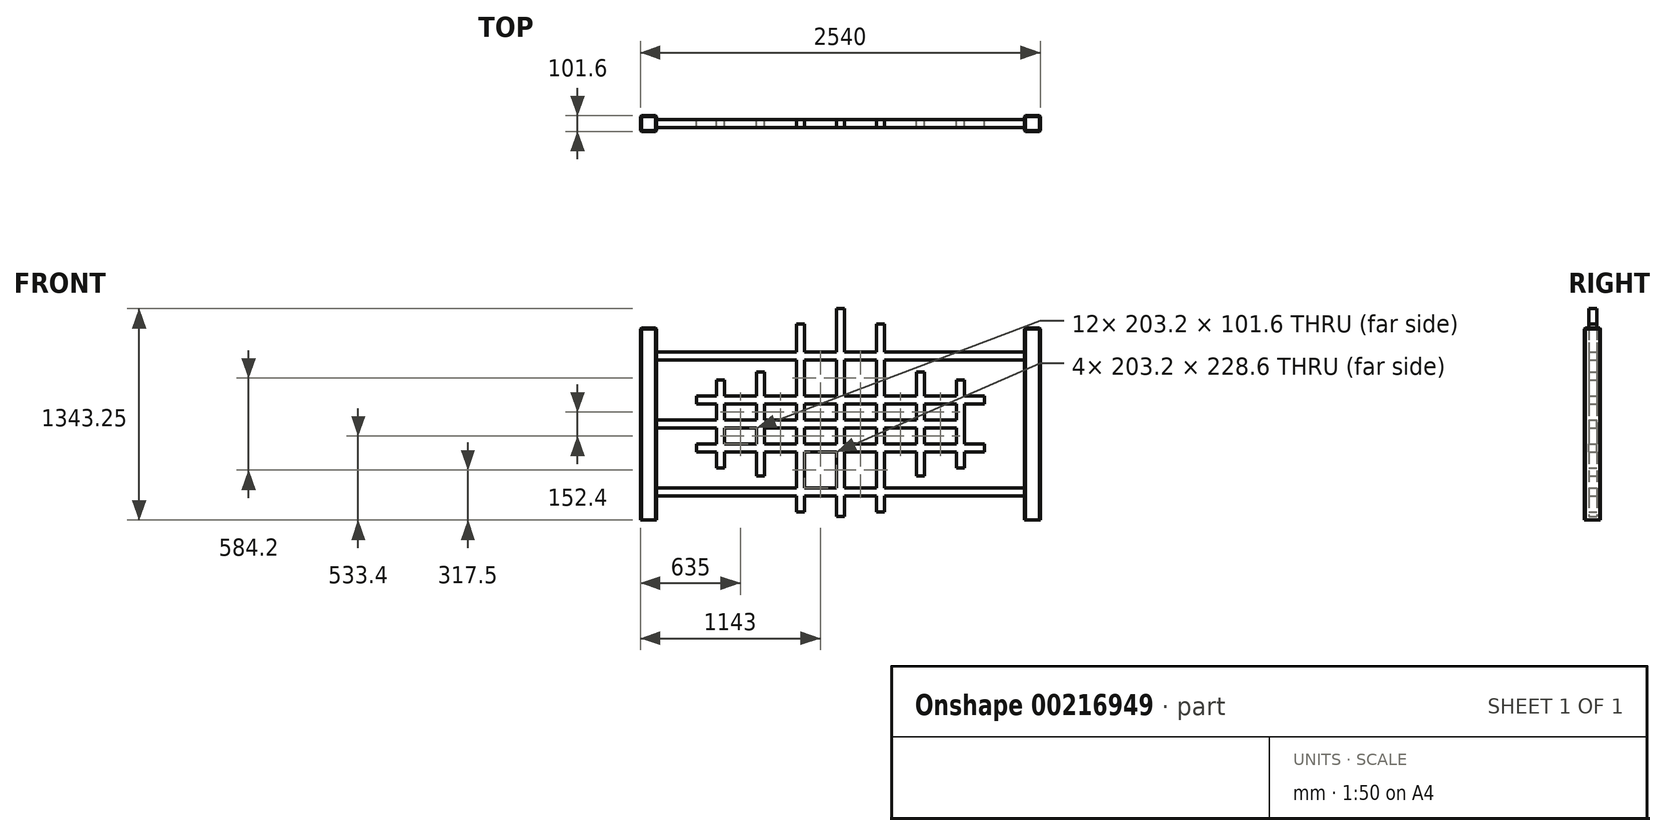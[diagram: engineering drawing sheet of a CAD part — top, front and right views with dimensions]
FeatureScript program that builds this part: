
annotation { "Feature Type Name" : "Feature", "Feature Type Description" : "" }
export const myFeature = defineFeature(function(context is Context, id is Id, definition is map)
    precondition{}
    {
        {
            var Q0;
            Q0=qCreatedBy(makeId("Front.planeOp"),FACE);
            var sketch = newSketch(context, id + "F0", { "sketchPlane" : qUnion([Q0])});
            skLineSegment(sketch, "E0", {"start": v(0, 0) * mm, "end": v(50.8, 0) * mm});
            skLineSegment(sketch, "E1", {"start": v(50.8, 0) * mm, "end": v(50.8, 1219.2) * mm});
            skLineSegment(sketch, "E2", {"start": v(50.8, 1219.2) * mm, "end": v(-50.8, 1219.2) * mm});
            skLineSegment(sketch, "E3", {"start": v(-50.8, 1219.2) * mm, "end": v(-50.8, 0) * mm});
            skLineSegment(sketch, "E4", {"start": v(-50.8, 0) * mm, "end": v(0, 0) * mm});
            skLineSegment(sketch, "E5", {"start": v(-50.8, 609.6) * mm, "end": v(-50.8, 152.4) * mm});
            skLineSegment(sketch, "E6", {"start": v(-50.8, 152.4) * mm, "end": v(-2387.6, 152.4) * mm});
            skLineSegment(sketch, "E7", {"start": v(-2387.6, 152.4) * mm, "end": v(-2387.6, 203.2) * mm});
            skLineSegment(sketch, "E8", {"start": v(-2387.6, 203.2) * mm, "end": v(-50.8, 203.2) * mm});
            skLineSegment(sketch, "E9", {"start": v(-50.8, 203.2) * mm, "end": v(-50.8, 152.4) * mm});
            skLineSegment(sketch, "E10", {"start": v(-50.8, 609.6) * mm, "end": v(-50.8, 1016) * mm});
            skLineSegment(sketch, "E11", {"start": v(-50.8, 1016) * mm, "end": v(-2387.6, 1016) * mm});
            skLineSegment(sketch, "E12", {"start": v(-2387.6, 1016) * mm, "end": v(-2387.6, 1066.8) * mm});
            skLineSegment(sketch, "E13", {"start": v(-2387.6, 1066.8) * mm, "end": v(-50.8, 1066.8) * mm});
            skLineSegment(sketch, "E14", {"start": v(-50.8, 1066.8) * mm, "end": v(-50.8, 1016) * mm});
            skLineSegment(sketch, "E15", {"start": v(-2387.6, 0) * mm, "end": v(-2387.6, 1219.2) * mm});
            skLineSegment(sketch, "E16", {"start": v(-2387.6, 1219.2) * mm, "end": v(-2489.2, 1219.2) * mm});
            skLineSegment(sketch, "E17", {"start": v(-2489.2, 1219.2) * mm, "end": v(-2489.2, 0) * mm});
            skLineSegment(sketch, "E18", {"start": v(-2489.2, 0) * mm, "end": v(-2387.6, 0) * mm});
            skLineSegment(sketch, "E19.bottom", {"start": v(-2133.6, 787.4) * mm, "end": v(-304.8, 787.4) * mm});
            skLineSegment(sketch, "E19.top", {"start": v(-2133.6, 736.6) * mm, "end": v(-304.8, 736.6) * mm});
            skLineSegment(sketch, "E19.left", {"start": v(-2133.6, 787.4) * mm, "end": v(-2133.6, 736.6) * mm});
            skLineSegment(sketch, "E19.right", {"start": v(-304.8, 787.4) * mm, "end": v(-304.8, 736.6) * mm});
            skLineSegment(sketch, "E20.bottom", {"start": v(-2133.6, 431.8) * mm, "end": v(-304.8, 431.8) * mm});
            skLineSegment(sketch, "E20.top", {"start": v(-2133.6, 482.6) * mm, "end": v(-304.8, 482.6) * mm});
            skLineSegment(sketch, "E20.left", {"start": v(-2133.6, 431.8) * mm, "end": v(-2133.6, 482.6) * mm});
            skLineSegment(sketch, "E20.right", {"start": v(-304.8, 431.8) * mm, "end": v(-304.8, 482.6) * mm});
            skLineSegment(sketch, "E21.bottom", {"start": v(-1498.6, 1244.6) * mm, "end": v(-1447.8, 1244.6) * mm});
            skLineSegment(sketch, "E21.top", {"start": v(-1498.6, 50.8) * mm, "end": v(-1447.8, 50.8) * mm});
            skLineSegment(sketch, "E21.left", {"start": v(-1498.6, 1244.6) * mm, "end": v(-1498.6, 50.8) * mm});
            skLineSegment(sketch, "E21.right", {"start": v(-1447.8, 1244.6) * mm, "end": v(-1447.8, 50.8) * mm});
            skLineSegment(sketch, "E22.bottom", {"start": v(-990.6, 1244.6) * mm, "end": v(-939.8, 1244.6) * mm});
            skLineSegment(sketch, "E22.top", {"start": v(-990.6, 50.8) * mm, "end": v(-939.8, 50.8) * mm});
            skLineSegment(sketch, "E22.left", {"start": v(-990.6, 1244.6) * mm, "end": v(-990.6, 50.8) * mm});
            skLineSegment(sketch, "E22.right", {"start": v(-939.8, 1244.6) * mm, "end": v(-939.8, 50.8) * mm});
            skLineSegment(sketch, "E23.bottom", {"start": v(-1752.6, 939.8) * mm, "end": v(-1701.8, 939.8) * mm});
            skLineSegment(sketch, "E23.top", {"start": v(-1752.6, 279.4) * mm, "end": v(-1701.8, 279.4) * mm});
            skLineSegment(sketch, "E23.left", {"start": v(-1752.6, 939.8) * mm, "end": v(-1752.6, 279.4) * mm});
            skLineSegment(sketch, "E23.right", {"start": v(-1701.8, 939.8) * mm, "end": v(-1701.8, 279.4) * mm});
            skLineSegment(sketch, "E24", {"start": v(-2489.2, 609.6) * mm, "end": v(974.84, 609.6) * mm, "construction": true});
            skLineSegment(sketch, "E25", {"start": v(974.84, 609.6) * mm, "end": v(-3986.95, 609.6) * mm, "construction": true});
            skLineSegment(sketch, "E26", {"start": v(-1219.2, 1513.32) * mm, "end": v(-1219.2, -329.5) * mm, "construction": true});
            skPoint(sketch, "E26.startSnap0", {"position": v(-1219.2, 1066.8) * mm});
            skLineSegment(sketch, "E27.bottom", {"start": v(-736.6, 939.8) * mm, "end": v(-685.8, 939.8) * mm});
            skLineSegment(sketch, "E27.top", {"start": v(-736.6, 279.4) * mm, "end": v(-685.8, 279.4) * mm});
            skLineSegment(sketch, "E27.left", {"start": v(-736.6, 939.8) * mm, "end": v(-736.6, 279.4) * mm});
            skLineSegment(sketch, "E27.right", {"start": v(-685.8, 939.8) * mm, "end": v(-685.8, 279.4) * mm});
            skLineSegment(sketch, "E28.bottom", {"start": v(-2006.6, 889) * mm, "end": v(-1955.8, 889) * mm});
            skLineSegment(sketch, "E28.top", {"start": v(-2006.6, 330.2) * mm, "end": v(-1955.8, 330.2) * mm});
            skLineSegment(sketch, "E28.left", {"start": v(-2006.6, 889) * mm, "end": v(-2006.6, 635) * mm});
            skLineSegment(sketch, "E28.right", {"start": v(-1955.8, 889) * mm, "end": v(-1955.8, 330.2) * mm});
            skLineSegment(sketch, "E29.bottom", {"start": v(-482.6, 889) * mm, "end": v(-431.8, 889) * mm});
            skLineSegment(sketch, "E29.top", {"start": v(-482.6, 330.2) * mm, "end": v(-431.8, 330.2) * mm});
            skLineSegment(sketch, "E29.left", {"start": v(-482.6, 889) * mm, "end": v(-482.6, 330.2) * mm});
            skLineSegment(sketch, "E29.right", {"start": v(-431.8, 889) * mm, "end": v(-431.8, 330.2) * mm});
            skLineSegment(sketch, "E30.left", {"start": v(-2006.6, 635) * mm, "end": v(-2006.6, 584.2) * mm});
            skLineSegment(sketch, "E31.bottom", {"start": v(-1193.8, 1343.25) * mm, "end": v(-1244.6, 1343.25) * mm});
            skLineSegment(sketch, "E31.top", {"start": v(-1193.8, 22.45) * mm, "end": v(-1244.6, 22.45) * mm});
            skLineSegment(sketch, "E31.left", {"start": v(-1193.8, 1343.25) * mm, "end": v(-1193.8, 22.45) * mm});
            skLineSegment(sketch, "E31.right", {"start": v(-1244.6, 1343.25) * mm, "end": v(-1244.6, 22.45) * mm});
            skLineSegment(sketch, "E32.trimOffspring", {"start": v(-2006.6, 584.2) * mm, "end": v(-2006.6, 330.2) * mm});
            skLineSegment(sketch, "E33.bottom", {"start": v(-50.8, 584.2) * mm, "end": v(-2387.6, 584.2) * mm});
            skLineSegment(sketch, "E33.top", {"start": v(-50.8, 635) * mm, "end": v(-2387.6, 635) * mm});
            skLineSegment(sketch, "E33.right", {"start": v(-2387.6, 584.2) * mm, "end": v(-2387.6, 635) * mm});
            skPoint(sketch, "E33.middle", {"position": v(-1219.2, 609.6) * mm});
            skSolve(sketch);
        }
        {
            var Q0;
            Q0 = qSketchRegion(id + "F0", true);
            var Q1;
            {var subQ0=sQuery(id+"F0.wireOp",EDGE,"E19.left");Q1=makeQuery(id+"F0.imprint","IMPRINT",FACE,{"disambiguationData":[TD([[makeQuery(id+"F0.imprint","IMPRINT",EDGE,{"derivedFrom":subQ0}),1.0]])]});}
            var Q2;
            {var subQ0=sQuery(id+"F0.wireOp",EDGE,"E28.right");var subQ1=sQuery(id+"F0.wireOp",EDGE,"E19.bottom");var subQ2=makeQuery(id+"F0.imprint","INTERSECT",VERTEX,{"derivedFrom":[subQ1,subQ0]});Q2=makeQuery(id+"F0.imprint","IMPRINT",FACE,{"disambiguationData":[TD([[makeQuery(id+"F0.imprint","IMPRINT",EDGE,{"disambiguationData":[TD([[subQ2,-1.0]])],"derivedFrom":subQ1}),-1.0]])]});}
            var Q3;
            {var subQ0=sQuery(id+"F0.wireOp",EDGE,"E23.right");var subQ1=sQuery(id+"F0.wireOp",EDGE,"E19.bottom");var subQ2=makeQuery(id+"F0.imprint","INTERSECT",VERTEX,{"derivedFrom":[subQ1,subQ0]});Q3=makeQuery(id+"F0.imprint","IMPRINT",FACE,{"disambiguationData":[TD([[makeQuery(id+"F0.imprint","IMPRINT",EDGE,{"disambiguationData":[TD([[subQ2,-1.0]])],"derivedFrom":subQ1}),-1.0]])]});}
            var Q4;
            {var subQ0=sQuery(id+"F0.wireOp",EDGE,"E20.left");Q4=makeQuery(id+"F0.imprint","IMPRINT",FACE,{"disambiguationData":[TD([[makeQuery(id+"F0.imprint","IMPRINT",EDGE,{"derivedFrom":subQ0}),-1.0]])]});}
            var Q5;
            Q5=makeQuery(id+"F0.imprint","IMPRINT",FACE,{"disambiguationData":[TD([[makeQuery(id+"F0.imprint","IMPRINT",EDGE,{"derivedFrom":sQuery(id+"F0.wireOp",EDGE,"E30.bottom")}),1.0]])]});
            var Q6;
            {var subQ0=sQuery(id+"F0.wireOp",EDGE,"E28.left");var subQ1=sQuery(id+"F0.wireOp",EDGE,"E20.bottom");var subQ2=makeQuery(id+"F0.imprint","INTERSECT",VERTEX,{"derivedFrom":[subQ1,subQ0]});Q6=makeQuery(id+"F0.imprint","IMPRINT",FACE,{"disambiguationData":[TD([[makeQuery(id+"F0.imprint","IMPRINT",EDGE,{"disambiguationData":[TD([[subQ2,-1.0]])],"derivedFrom":subQ1}),1.0]])]});}
            var Q7;
            {var subQ0=sQuery(id+"F0.wireOp",EDGE,"E30.left");Q7=makeQuery(id+"F0.imprint","IMPRINT",FACE,{"disambiguationData":[TD([[makeQuery(id+"F0.imprint","IMPRINT",EDGE,{"derivedFrom":subQ0}),1.0]])]});}
            var Q8;
            {var subQ0=sQuery(id+"F0.wireOp",EDGE,"E28.left");var subQ1=sQuery(id+"F0.wireOp",EDGE,"E19.bottom");var subQ2=makeQuery(id+"F0.imprint","INTERSECT",VERTEX,{"derivedFrom":[subQ1,subQ0]});Q8=makeQuery(id+"F0.imprint","IMPRINT",FACE,{"disambiguationData":[TD([[makeQuery(id+"F0.imprint","IMPRINT",EDGE,{"disambiguationData":[TD([[subQ2,-1.0]])],"derivedFrom":subQ1}),-1.0]])]});}
            var Q9;
            {var subQ5=sQuery(id+"F0.wireOp",EDGE,"E28.bottom");Q9=makeQuery(id+"F0.imprint","IMPRINT",FACE,{"disambiguationData":[TD([[makeQuery(id+"F0.imprint","IMPRINT",EDGE,{"derivedFrom":subQ5}),-1.0]])]});}
            var Q10;
            {var subQ5=sQuery(id+"F0.wireOp",EDGE,"E28.top");Q10=makeQuery(id+"F0.imprint","IMPRINT",FACE,{"disambiguationData":[TD([[makeQuery(id+"F0.imprint","IMPRINT",EDGE,{"derivedFrom":subQ5}),1.0]])]});}
            var Q11;
            {var subQ0=sQuery(id+"F0.wireOp",EDGE,"E28.right");var subQ1=sQuery(id+"F0.wireOp",EDGE,"E20.bottom");var subQ2=makeQuery(id+"F0.imprint","INTERSECT",VERTEX,{"derivedFrom":[subQ1,subQ0]});Q11=makeQuery(id+"F0.imprint","IMPRINT",FACE,{"disambiguationData":[TD([[makeQuery(id+"F0.imprint","IMPRINT",EDGE,{"disambiguationData":[TD([[subQ2,-1.0]])],"derivedFrom":subQ1}),1.0]])]});}
            var Q12;
            {var subQ0=sQuery(id+"F0.wireOp",EDGE,"E23.left");var subQ1=sQuery(id+"F0.wireOp",EDGE,"E20.bottom");var subQ2=makeQuery(id+"F0.imprint","INTERSECT",VERTEX,{"derivedFrom":[subQ1,subQ0]});Q12=makeQuery(id+"F0.imprint","IMPRINT",FACE,{"disambiguationData":[TD([[makeQuery(id+"F0.imprint","IMPRINT",EDGE,{"disambiguationData":[TD([[subQ2,-1.0]])],"derivedFrom":subQ1}),1.0]])]});}
            var Q13;
            {var subQ0=sQuery(id+"F0.wireOp",EDGE,"E23.right");var subQ1=sQuery(id+"F0.wireOp",EDGE,"E20.bottom");var subQ2=makeQuery(id+"F0.imprint","INTERSECT",VERTEX,{"derivedFrom":[subQ1,subQ0]});Q13=makeQuery(id+"F0.imprint","IMPRINT",FACE,{"disambiguationData":[TD([[makeQuery(id+"F0.imprint","IMPRINT",EDGE,{"disambiguationData":[TD([[subQ2,-1.0]])],"derivedFrom":subQ1}),1.0]])]});}
            var Q14;
            {var subQ0=sQuery(id+"F0.wireOp",EDGE,"E21.left");var subQ1=sQuery(id+"F0.wireOp",EDGE,"E20.bottom");var subQ2=makeQuery(id+"F0.imprint","INTERSECT",VERTEX,{"derivedFrom":[subQ1,subQ0]});Q14=makeQuery(id+"F0.imprint","IMPRINT",FACE,{"disambiguationData":[TD([[makeQuery(id+"F0.imprint","IMPRINT",EDGE,{"disambiguationData":[TD([[subQ2,-1.0]])],"derivedFrom":subQ1}),1.0]])]});}
            var Q15;
            {var subQ0=sQuery(id+"F0.wireOp",EDGE,"E21.right");var subQ1=sQuery(id+"F0.wireOp",EDGE,"E20.bottom");var subQ2=makeQuery(id+"F0.imprint","INTERSECT",VERTEX,{"derivedFrom":[subQ1,subQ0]});Q15=makeQuery(id+"F0.imprint","IMPRINT",FACE,{"disambiguationData":[TD([[makeQuery(id+"F0.imprint","IMPRINT",EDGE,{"disambiguationData":[TD([[subQ2,-1.0]])],"derivedFrom":subQ1}),1.0]])]});}
            var Q16;
            {var subQ0=sQuery(id+"F0.wireOp",EDGE,"E22.left");var subQ1=sQuery(id+"F0.wireOp",EDGE,"E20.bottom");var subQ2=makeQuery(id+"F0.imprint","INTERSECT",VERTEX,{"derivedFrom":[subQ1,subQ0]});Q16=makeQuery(id+"F0.imprint","IMPRINT",FACE,{"disambiguationData":[TD([[makeQuery(id+"F0.imprint","IMPRINT",EDGE,{"disambiguationData":[TD([[subQ2,-1.0]])],"derivedFrom":subQ1}),1.0]])]});}
            var Q17;
            {var subQ0=sQuery(id+"F0.wireOp",EDGE,"E22.right");var subQ1=sQuery(id+"F0.wireOp",EDGE,"E20.bottom");var subQ2=makeQuery(id+"F0.imprint","INTERSECT",VERTEX,{"derivedFrom":[subQ1,subQ0]});Q17=makeQuery(id+"F0.imprint","IMPRINT",FACE,{"disambiguationData":[TD([[makeQuery(id+"F0.imprint","IMPRINT",EDGE,{"disambiguationData":[TD([[subQ2,-1.0]])],"derivedFrom":subQ1}),1.0]])]});}
            var Q18;
            {var subQ0=sQuery(id+"F0.wireOp",EDGE,"E27.left");var subQ1=sQuery(id+"F0.wireOp",EDGE,"E20.bottom");var subQ2=makeQuery(id+"F0.imprint","INTERSECT",VERTEX,{"derivedFrom":[subQ1,subQ0]});Q18=makeQuery(id+"F0.imprint","IMPRINT",FACE,{"disambiguationData":[TD([[makeQuery(id+"F0.imprint","IMPRINT",EDGE,{"disambiguationData":[TD([[subQ2,-1.0]])],"derivedFrom":subQ1}),1.0]])]});}
            var Q19;
            {var subQ0=sQuery(id+"F0.wireOp",EDGE,"E27.right");var subQ1=sQuery(id+"F0.wireOp",EDGE,"E20.bottom");var subQ2=makeQuery(id+"F0.imprint","INTERSECT",VERTEX,{"derivedFrom":[subQ1,subQ0]});Q19=makeQuery(id+"F0.imprint","IMPRINT",FACE,{"disambiguationData":[TD([[makeQuery(id+"F0.imprint","IMPRINT",EDGE,{"disambiguationData":[TD([[subQ2,-1.0]])],"derivedFrom":subQ1}),1.0]])]});}
            var Q20;
            {var subQ0=sQuery(id+"F0.wireOp",EDGE,"E29.left");var subQ1=sQuery(id+"F0.wireOp",EDGE,"E20.bottom");var subQ2=makeQuery(id+"F0.imprint","INTERSECT",VERTEX,{"derivedFrom":[subQ1,subQ0]});Q20=makeQuery(id+"F0.imprint","IMPRINT",FACE,{"disambiguationData":[TD([[makeQuery(id+"F0.imprint","IMPRINT",EDGE,{"disambiguationData":[TD([[subQ2,-1.0]])],"derivedFrom":subQ1}),1.0]])]});}
            var Q21;
            {var subQ0=sQuery(id+"F0.wireOp",EDGE,"E20.right");Q21=makeQuery(id+"F0.imprint","IMPRINT",FACE,{"disambiguationData":[TD([[makeQuery(id+"F0.imprint","IMPRINT",EDGE,{"derivedFrom":subQ0}),1.0]])]});}
            var Q22;
            Q22=makeQuery(id+"F0.imprint","IMPRINT",FACE,{"disambiguationData":[TD([[makeQuery(id+"F0.imprint","IMPRINT",EDGE,{"derivedFrom":sQuery(id+"F0.wireOp",EDGE,"NliR9Cyk-CJk0-Iiul-wSK4-aNZwnmZK0H1W.bottom")}),-1.0]])]});
            var Q23;
            {var subQ0=sQuery(id+"F0.wireOp",EDGE,"E19.right");Q23=makeQuery(id+"F0.imprint","IMPRINT",FACE,{"disambiguationData":[TD([[makeQuery(id+"F0.imprint","IMPRINT",EDGE,{"derivedFrom":subQ0}),-1.0]])]});}
            var Q24;
            {var subQ0=sQuery(id+"F0.wireOp",EDGE,"E29.left");var subQ1=sQuery(id+"F0.wireOp",EDGE,"E19.bottom");var subQ2=makeQuery(id+"F0.imprint","INTERSECT",VERTEX,{"derivedFrom":[subQ1,subQ0]});Q24=makeQuery(id+"F0.imprint","IMPRINT",FACE,{"disambiguationData":[TD([[makeQuery(id+"F0.imprint","IMPRINT",EDGE,{"disambiguationData":[TD([[subQ2,-1.0]])],"derivedFrom":subQ1}),-1.0]])]});}
            var Q25;
            {var subQ0=sQuery(id+"F0.wireOp",EDGE,"E27.right");var subQ1=sQuery(id+"F0.wireOp",EDGE,"E19.bottom");var subQ2=makeQuery(id+"F0.imprint","INTERSECT",VERTEX,{"derivedFrom":[subQ1,subQ0]});Q25=makeQuery(id+"F0.imprint","IMPRINT",FACE,{"disambiguationData":[TD([[makeQuery(id+"F0.imprint","IMPRINT",EDGE,{"disambiguationData":[TD([[subQ2,-1.0]])],"derivedFrom":subQ1}),-1.0]])]});}
            var Q26;
            {var subQ0=sQuery(id+"F0.wireOp",EDGE,"E27.left");var subQ1=sQuery(id+"F0.wireOp",EDGE,"E19.bottom");var subQ2=makeQuery(id+"F0.imprint","INTERSECT",VERTEX,{"derivedFrom":[subQ1,subQ0]});Q26=makeQuery(id+"F0.imprint","IMPRINT",FACE,{"disambiguationData":[TD([[makeQuery(id+"F0.imprint","IMPRINT",EDGE,{"disambiguationData":[TD([[subQ2,-1.0]])],"derivedFrom":subQ1}),-1.0]])]});}
            var Q27;
            {var subQ0=sQuery(id+"F0.wireOp",EDGE,"E22.right");var subQ1=sQuery(id+"F0.wireOp",EDGE,"E19.bottom");var subQ2=makeQuery(id+"F0.imprint","INTERSECT",VERTEX,{"derivedFrom":[subQ1,subQ0]});Q27=makeQuery(id+"F0.imprint","IMPRINT",FACE,{"disambiguationData":[TD([[makeQuery(id+"F0.imprint","IMPRINT",EDGE,{"disambiguationData":[TD([[subQ2,-1.0]])],"derivedFrom":subQ1}),-1.0]])]});}
            var Q28;
            {var subQ0=sQuery(id+"F0.wireOp",EDGE,"E22.left");var subQ1=sQuery(id+"F0.wireOp",EDGE,"E19.bottom");var subQ2=makeQuery(id+"F0.imprint","INTERSECT",VERTEX,{"derivedFrom":[subQ1,subQ0]});Q28=makeQuery(id+"F0.imprint","IMPRINT",FACE,{"disambiguationData":[TD([[makeQuery(id+"F0.imprint","IMPRINT",EDGE,{"disambiguationData":[TD([[subQ2,-1.0]])],"derivedFrom":subQ1}),-1.0]])]});}
            var Q29;
            {var subQ0=sQuery(id+"F0.wireOp",EDGE,"E21.right");var subQ1=sQuery(id+"F0.wireOp",EDGE,"E19.bottom");var subQ2=makeQuery(id+"F0.imprint","INTERSECT",VERTEX,{"derivedFrom":[subQ1,subQ0]});Q29=makeQuery(id+"F0.imprint","IMPRINT",FACE,{"disambiguationData":[TD([[makeQuery(id+"F0.imprint","IMPRINT",EDGE,{"disambiguationData":[TD([[subQ2,-1.0]])],"derivedFrom":subQ1}),-1.0]])]});}
            var Q30;
            {var subQ0=sQuery(id+"F0.wireOp",EDGE,"E21.left");var subQ1=sQuery(id+"F0.wireOp",EDGE,"E19.bottom");var subQ2=makeQuery(id+"F0.imprint","INTERSECT",VERTEX,{"derivedFrom":[subQ1,subQ0]});Q30=makeQuery(id+"F0.imprint","IMPRINT",FACE,{"disambiguationData":[TD([[makeQuery(id+"F0.imprint","IMPRINT",EDGE,{"disambiguationData":[TD([[subQ2,-1.0]])],"derivedFrom":subQ1}),-1.0]])]});}
            var Q31;
            {var subQ0=sQuery(id+"F0.wireOp",EDGE,"E23.left");var subQ1=sQuery(id+"F0.wireOp",EDGE,"E19.bottom");var subQ2=makeQuery(id+"F0.imprint","INTERSECT",VERTEX,{"derivedFrom":[subQ1,subQ0]});Q31=makeQuery(id+"F0.imprint","IMPRINT",FACE,{"disambiguationData":[TD([[makeQuery(id+"F0.imprint","IMPRINT",EDGE,{"disambiguationData":[TD([[subQ2,-1.0]])],"derivedFrom":subQ1}),-1.0]])]});}
            var Q32;
            {var subQ5=sQuery(id+"F0.wireOp",EDGE,"E23.bottom");Q32=makeQuery(id+"F0.imprint","IMPRINT",FACE,{"disambiguationData":[TD([[makeQuery(id+"F0.imprint","IMPRINT",EDGE,{"derivedFrom":subQ5}),-1.0]])]});}
            var Q33;
            {var subQ5=sQuery(id+"F0.wireOp",EDGE,"E23.top");Q33=makeQuery(id+"F0.imprint","IMPRINT",FACE,{"disambiguationData":[TD([[makeQuery(id+"F0.imprint","IMPRINT",EDGE,{"derivedFrom":subQ5}),1.0]])]});}
            var Q34;
            {var subQ0=sQuery(id+"F0.wireOp",EDGE,"E21.left");var subQ1=sQuery(id+"F0.wireOp",EDGE,"E8");var subQ2=makeQuery(id+"F0.imprint","INTERSECT",VERTEX,{"derivedFrom":[subQ1,subQ0]});Q34=makeQuery(id+"F0.imprint","IMPRINT",FACE,{"disambiguationData":[TD([[makeQuery(id+"F0.imprint","IMPRINT",EDGE,{"disambiguationData":[TD([[subQ2,-1.0]])],"derivedFrom":subQ1}),1.0]])]});}
            var Q35;
            {var subQ0=sQuery(id+"F0.wireOp",EDGE,"E22.left");var subQ1=sQuery(id+"F0.wireOp",EDGE,"E8");var subQ2=makeQuery(id+"F0.imprint","INTERSECT",VERTEX,{"derivedFrom":[subQ1,subQ0]});Q35=makeQuery(id+"F0.imprint","IMPRINT",FACE,{"disambiguationData":[TD([[makeQuery(id+"F0.imprint","IMPRINT",EDGE,{"disambiguationData":[TD([[subQ2,-1.0]])],"derivedFrom":subQ1}),1.0]])]});}
            var Q36;
            {var subQ5=sQuery(id+"F0.wireOp",EDGE,"E27.top");Q36=makeQuery(id+"F0.imprint","IMPRINT",FACE,{"disambiguationData":[TD([[makeQuery(id+"F0.imprint","IMPRINT",EDGE,{"derivedFrom":subQ5}),1.0]])]});}
            var Q37;
            {var subQ5=sQuery(id+"F0.wireOp",EDGE,"E29.top");Q37=makeQuery(id+"F0.imprint","IMPRINT",FACE,{"disambiguationData":[TD([[makeQuery(id+"F0.imprint","IMPRINT",EDGE,{"derivedFrom":subQ5}),1.0]])]});}
            var Q38;
            {var subQ0=sQuery(id+"F0.wireOp",EDGE,"NliR9Cyk-CJk0-Iiul-wSK4-aNZwnmZK0H1W.left");Q38=makeQuery(id+"F0.imprint","IMPRINT",FACE,{"disambiguationData":[TD([[makeQuery(id+"F0.imprint","IMPRINT",EDGE,{"derivedFrom":subQ0}),-1.0]])]});}
            var Q39;
            {var subQ0=sQuery(id+"F0.wireOp",EDGE,"E27.left");var subQ1=sQuery(id+"F0.wireOp",EDGE,"E19.top");var subQ2=makeQuery(id+"F0.imprint","INTERSECT",VERTEX,{"derivedFrom":[subQ1,subQ0]});Q39=makeQuery(id+"F0.imprint","IMPRINT",FACE,{"disambiguationData":[TD([[makeQuery(id+"F0.imprint","IMPRINT",EDGE,{"disambiguationData":[TD([[subQ2,-1.0]])],"derivedFrom":subQ1}),-1.0]])]});}
            var Q40;
            {var subQ0=sQuery(id+"F0.wireOp",EDGE,"E22.left");var subQ1=sQuery(id+"F0.wireOp",EDGE,"E19.top");var subQ2=makeQuery(id+"F0.imprint","INTERSECT",VERTEX,{"derivedFrom":[subQ1,subQ0]});Q40=makeQuery(id+"F0.imprint","IMPRINT",FACE,{"disambiguationData":[TD([[makeQuery(id+"F0.imprint","IMPRINT",EDGE,{"disambiguationData":[TD([[subQ2,-1.0]])],"derivedFrom":subQ1}),-1.0]])]});}
            var Q41;
            {var subQ0=sQuery(id+"F0.wireOp",EDGE,"E21.left");var subQ1=sQuery(id+"F0.wireOp",EDGE,"E19.top");var subQ2=makeQuery(id+"F0.imprint","INTERSECT",VERTEX,{"derivedFrom":[subQ1,subQ0]});Q41=makeQuery(id+"F0.imprint","IMPRINT",FACE,{"disambiguationData":[TD([[makeQuery(id+"F0.imprint","IMPRINT",EDGE,{"disambiguationData":[TD([[subQ2,-1.0]])],"derivedFrom":subQ1}),-1.0]])]});}
            var Q42;
            {var subQ0=sQuery(id+"F0.wireOp",EDGE,"E23.left");var subQ1=sQuery(id+"F0.wireOp",EDGE,"E19.top");var subQ2=makeQuery(id+"F0.imprint","INTERSECT",VERTEX,{"derivedFrom":[subQ1,subQ0]});Q42=makeQuery(id+"F0.imprint","IMPRINT",FACE,{"disambiguationData":[TD([[makeQuery(id+"F0.imprint","IMPRINT",EDGE,{"disambiguationData":[TD([[subQ2,-1.0]])],"derivedFrom":subQ1}),-1.0]])]});}
            var Q43;
            {var subQ0=sQuery(id+"F0.wireOp",EDGE,"E21.right");var subQ1=sQuery(id+"F0.wireOp",EDGE,"E11");var subQ2=makeQuery(id+"F0.imprint","INTERSECT",VERTEX,{"derivedFrom":[subQ1,subQ0]});Q43=makeQuery(id+"F0.imprint","IMPRINT",FACE,{"disambiguationData":[TD([[makeQuery(id+"F0.imprint","IMPRINT",EDGE,{"disambiguationData":[TD([[subQ2,-1.0]])],"derivedFrom":subQ1}),1.0]])]});}
            var Q44;
            {var subQ0=sQuery(id+"F0.wireOp",EDGE,"E22.right");var subQ1=sQuery(id+"F0.wireOp",EDGE,"E11");var subQ2=makeQuery(id+"F0.imprint","INTERSECT",VERTEX,{"derivedFrom":[subQ1,subQ0]});Q44=makeQuery(id+"F0.imprint","IMPRINT",FACE,{"disambiguationData":[TD([[makeQuery(id+"F0.imprint","IMPRINT",EDGE,{"disambiguationData":[TD([[subQ2,-1.0]])],"derivedFrom":subQ1}),1.0]])]});}
            var Q45;
            {var subQ5=sQuery(id+"F0.wireOp",EDGE,"E27.bottom");Q45=makeQuery(id+"F0.imprint","IMPRINT",FACE,{"disambiguationData":[TD([[makeQuery(id+"F0.imprint","IMPRINT",EDGE,{"derivedFrom":subQ5}),-1.0]])]});}
            var Q46;
            {var subQ5=sQuery(id+"F0.wireOp",EDGE,"E29.bottom");Q46=makeQuery(id+"F0.imprint","IMPRINT",FACE,{"disambiguationData":[TD([[makeQuery(id+"F0.imprint","IMPRINT",EDGE,{"derivedFrom":subQ5}),-1.0]])]});}
            var Q47;
            {var subQ1=sQuery(id+"F0.wireOp",EDGE,"E5");var subQ7=sQuery(id+"F0.wireOp",EDGE,"E10");var subQ8=makeQuery(id+"F0.imprint","INTERSECT",VERTEX,{"derivedFrom":[subQ1,subQ7]});Q47=makeQuery(id+"F0.imprint","IMPRINT",FACE,{"disambiguationData":[TD([[makeQuery(id+"F0.imprint","IMPRINT",EDGE,{"disambiguationData":[TD([[subQ8,-1.0]])],"derivedFrom":subQ1}),-1.0]])]});}
            var Q48;
            {var subQ0=sQuery(id+"F0.wireOp",EDGE,"E33.top");var subQ1=sQuery(id+"F0.wireOp",EDGE,"E29.left");var subQ2=makeQuery(id+"F0.imprint","INTERSECT",VERTEX,{"derivedFrom":[subQ1,subQ0]});Q48=makeQuery(id+"F0.imprint","IMPRINT",FACE,{"disambiguationData":[TD([[makeQuery(id+"F0.imprint","IMPRINT",EDGE,{"disambiguationData":[TD([[subQ2,-1.0]])],"derivedFrom":subQ1}),1.0]])]});}
            var Q49;
            {var subQ0=sQuery(id+"F0.wireOp",EDGE,"E33.top");var subQ1=sQuery(id+"F0.wireOp",EDGE,"E27.right");var subQ2=makeQuery(id+"F0.imprint","INTERSECT",VERTEX,{"derivedFrom":[subQ1,subQ0]});Q49=makeQuery(id+"F0.imprint","IMPRINT",FACE,{"disambiguationData":[TD([[makeQuery(id+"F0.imprint","IMPRINT",EDGE,{"disambiguationData":[TD([[subQ2,-1.0]])],"derivedFrom":subQ1}),1.0]])]});}
            var Q50;
            {var subQ0=sQuery(id+"F0.wireOp",EDGE,"E33.top");var subQ1=sQuery(id+"F0.wireOp",EDGE,"E27.left");var subQ2=makeQuery(id+"F0.imprint","INTERSECT",VERTEX,{"derivedFrom":[subQ1,subQ0]});Q50=makeQuery(id+"F0.imprint","IMPRINT",FACE,{"disambiguationData":[TD([[makeQuery(id+"F0.imprint","IMPRINT",EDGE,{"disambiguationData":[TD([[subQ2,-1.0]])],"derivedFrom":subQ1}),1.0]])]});}
            var Q51;
            {var subQ0=sQuery(id+"F0.wireOp",EDGE,"E33.top");var subQ1=sQuery(id+"F0.wireOp",EDGE,"E22.right");var subQ2=makeQuery(id+"F0.imprint","INTERSECT",VERTEX,{"derivedFrom":[subQ1,subQ0]});Q51=makeQuery(id+"F0.imprint","IMPRINT",FACE,{"disambiguationData":[TD([[makeQuery(id+"F0.imprint","IMPRINT",EDGE,{"disambiguationData":[TD([[subQ2,-1.0]])],"derivedFrom":subQ1}),1.0]])]});}
            var Q52;
            {var subQ0=sQuery(id+"F0.wireOp",EDGE,"E33.top");var subQ1=sQuery(id+"F0.wireOp",EDGE,"E22.left");var subQ2=makeQuery(id+"F0.imprint","INTERSECT",VERTEX,{"derivedFrom":[subQ1,subQ0]});Q52=makeQuery(id+"F0.imprint","IMPRINT",FACE,{"disambiguationData":[TD([[makeQuery(id+"F0.imprint","IMPRINT",EDGE,{"disambiguationData":[TD([[subQ2,-1.0]])],"derivedFrom":subQ1}),1.0]])]});}
            var Q53;
            {var subQ0=sQuery(id+"F0.wireOp",EDGE,"E33.top");var subQ1=sQuery(id+"F0.wireOp",EDGE,"E22.left");var subQ2=makeQuery(id+"F0.imprint","INTERSECT",VERTEX,{"derivedFrom":[subQ1,subQ0]});Q53=makeQuery(id+"F0.imprint","IMPRINT",FACE,{"disambiguationData":[TD([[makeQuery(id+"F0.imprint","IMPRINT",EDGE,{"disambiguationData":[TD([[subQ2,-1.0]])],"derivedFrom":subQ1}),-1.0]])]});}
            var Q54;
            {var subQ0=sQuery(id+"F0.wireOp",EDGE,"E33.top");var subQ1=sQuery(id+"F0.wireOp",EDGE,"E31.left");var subQ2=makeQuery(id+"F0.imprint","INTERSECT",VERTEX,{"derivedFrom":[subQ1,subQ0]});Q54=makeQuery(id+"F0.imprint","IMPRINT",FACE,{"disambiguationData":[TD([[makeQuery(id+"F0.imprint","IMPRINT",EDGE,{"disambiguationData":[TD([[subQ2,-1.0]])],"derivedFrom":subQ1}),-1.0]])]});}
            var Q55;
            {var subQ0=sQuery(id+"F0.wireOp",EDGE,"E33.top");var subQ1=sQuery(id+"F0.wireOp",EDGE,"E21.right");var subQ2=makeQuery(id+"F0.imprint","INTERSECT",VERTEX,{"derivedFrom":[subQ1,subQ0]});Q55=makeQuery(id+"F0.imprint","IMPRINT",FACE,{"disambiguationData":[TD([[makeQuery(id+"F0.imprint","IMPRINT",EDGE,{"disambiguationData":[TD([[subQ2,-1.0]])],"derivedFrom":subQ1}),1.0]])]});}
            var Q56;
            {var subQ0=sQuery(id+"F0.wireOp",EDGE,"E33.top");var subQ1=sQuery(id+"F0.wireOp",EDGE,"E21.left");var subQ2=makeQuery(id+"F0.imprint","INTERSECT",VERTEX,{"derivedFrom":[subQ1,subQ0]});Q56=makeQuery(id+"F0.imprint","IMPRINT",FACE,{"disambiguationData":[TD([[makeQuery(id+"F0.imprint","IMPRINT",EDGE,{"disambiguationData":[TD([[subQ2,-1.0]])],"derivedFrom":subQ1}),1.0]])]});}
            var Q57;
            {var subQ0=sQuery(id+"F0.wireOp",EDGE,"E33.top");var subQ1=sQuery(id+"F0.wireOp",EDGE,"E21.left");var subQ2=makeQuery(id+"F0.imprint","INTERSECT",VERTEX,{"derivedFrom":[subQ1,subQ0]});Q57=makeQuery(id+"F0.imprint","IMPRINT",FACE,{"disambiguationData":[TD([[makeQuery(id+"F0.imprint","IMPRINT",EDGE,{"disambiguationData":[TD([[subQ2,-1.0]])],"derivedFrom":subQ1}),-1.0]])]});}
            var Q58;
            {var subQ0=sQuery(id+"F0.wireOp",EDGE,"E33.top");var subQ1=sQuery(id+"F0.wireOp",EDGE,"E23.left");var subQ2=makeQuery(id+"F0.imprint","INTERSECT",VERTEX,{"derivedFrom":[subQ1,subQ0]});Q58=makeQuery(id+"F0.imprint","IMPRINT",FACE,{"disambiguationData":[TD([[makeQuery(id+"F0.imprint","IMPRINT",EDGE,{"disambiguationData":[TD([[subQ2,-1.0]])],"derivedFrom":subQ1}),1.0]])]});}
            var Q59;
            {var subQ0=sQuery(id+"F0.wireOp",EDGE,"E33.top");var subQ1=sQuery(id+"F0.wireOp",EDGE,"E23.left");var subQ2=makeQuery(id+"F0.imprint","INTERSECT",VERTEX,{"derivedFrom":[subQ1,subQ0]});Q59=makeQuery(id+"F0.imprint","IMPRINT",FACE,{"disambiguationData":[TD([[makeQuery(id+"F0.imprint","IMPRINT",EDGE,{"disambiguationData":[TD([[subQ2,-1.0]])],"derivedFrom":subQ1}),-1.0]])]});}
            var Q60;
            {var subQ0=sQuery(id+"F0.wireOp",EDGE,"E30.left");Q60=makeQuery(id+"F0.imprint","IMPRINT",FACE,{"disambiguationData":[TD([[makeQuery(id+"F0.imprint","IMPRINT",EDGE,{"derivedFrom":subQ0}),-1.0]])]});}
            var Q61;
            {var subQ0=sQuery(id+"F0.wireOp",EDGE,"E32.trimOffspring");var subQ1=sQuery(id+"F0.wireOp",EDGE,"E20.top");var subQ2=makeQuery(id+"F0.imprint","INTERSECT",VERTEX,{"derivedFrom":[subQ1,subQ0]});Q61=makeQuery(id+"F0.imprint","IMPRINT",FACE,{"disambiguationData":[TD([[makeQuery(id+"F0.imprint","IMPRINT",EDGE,{"disambiguationData":[TD([[subQ2,-1.0]])],"derivedFrom":subQ1}),1.0]])]});}
            var Q62;
            {var subQ0=sQuery(id+"F0.wireOp",EDGE,"E28.left");var subQ1=sQuery(id+"F0.wireOp",EDGE,"E19.top");var subQ2=makeQuery(id+"F0.imprint","INTERSECT",VERTEX,{"derivedFrom":[subQ1,subQ0]});Q62=makeQuery(id+"F0.imprint","IMPRINT",FACE,{"disambiguationData":[TD([[makeQuery(id+"F0.imprint","IMPRINT",EDGE,{"disambiguationData":[TD([[subQ2,-1.0]])],"derivedFrom":subQ1}),-1.0]])]});}
            var Q63;
            {var subQ0=sQuery(id+"F0.wireOp",EDGE,"E23.left");var subQ1=sQuery(id+"F0.wireOp",EDGE,"E20.top");var subQ2=makeQuery(id+"F0.imprint","INTERSECT",VERTEX,{"derivedFrom":[subQ1,subQ0]});Q63=makeQuery(id+"F0.imprint","IMPRINT",FACE,{"disambiguationData":[TD([[makeQuery(id+"F0.imprint","IMPRINT",EDGE,{"disambiguationData":[TD([[subQ2,-1.0]])],"derivedFrom":subQ1}),1.0]])]});}
            var Q64;
            {var subQ0=sQuery(id+"F0.wireOp",EDGE,"E21.left");var subQ1=sQuery(id+"F0.wireOp",EDGE,"E20.top");var subQ2=makeQuery(id+"F0.imprint","INTERSECT",VERTEX,{"derivedFrom":[subQ1,subQ0]});Q64=makeQuery(id+"F0.imprint","IMPRINT",FACE,{"disambiguationData":[TD([[makeQuery(id+"F0.imprint","IMPRINT",EDGE,{"disambiguationData":[TD([[subQ2,-1.0]])],"derivedFrom":subQ1}),1.0]])]});}
            var Q65;
            {var subQ0=sQuery(id+"F0.wireOp",EDGE,"E31.left");var subQ1=sQuery(id+"F0.wireOp",EDGE,"E11");var subQ2=makeQuery(id+"F0.imprint","INTERSECT",VERTEX,{"derivedFrom":[subQ1,subQ0]});Q65=makeQuery(id+"F0.imprint","IMPRINT",FACE,{"disambiguationData":[TD([[makeQuery(id+"F0.imprint","IMPRINT",EDGE,{"disambiguationData":[TD([[subQ2,-1.0]])],"derivedFrom":subQ1}),1.0]])]});}
            var Q66;
            {var subQ0=sQuery(id+"F0.wireOp",EDGE,"E31.right");var subQ1=sQuery(id+"F0.wireOp",EDGE,"E19.top");var subQ2=makeQuery(id+"F0.imprint","INTERSECT",VERTEX,{"derivedFrom":[subQ1,subQ0]});Q66=makeQuery(id+"F0.imprint","IMPRINT",FACE,{"disambiguationData":[TD([[makeQuery(id+"F0.imprint","IMPRINT",EDGE,{"disambiguationData":[TD([[subQ2,-1.0]])],"derivedFrom":subQ1}),-1.0]])]});}
            var Q67;
            {var subQ0=sQuery(id+"F0.wireOp",EDGE,"E31.right");var subQ1=sQuery(id+"F0.wireOp",EDGE,"E19.bottom");var subQ2=makeQuery(id+"F0.imprint","INTERSECT",VERTEX,{"derivedFrom":[subQ1,subQ0]});Q67=makeQuery(id+"F0.imprint","IMPRINT",FACE,{"disambiguationData":[TD([[makeQuery(id+"F0.imprint","IMPRINT",EDGE,{"disambiguationData":[TD([[subQ2,-1.0]])],"derivedFrom":subQ1}),-1.0]])]});}
            var Q68;
            {var subQ0=sQuery(id+"F0.wireOp",EDGE,"E31.right");var subQ1=sQuery(id+"F0.wireOp",EDGE,"E20.top");var subQ2=makeQuery(id+"F0.imprint","INTERSECT",VERTEX,{"derivedFrom":[subQ1,subQ0]});Q68=makeQuery(id+"F0.imprint","IMPRINT",FACE,{"disambiguationData":[TD([[makeQuery(id+"F0.imprint","IMPRINT",EDGE,{"disambiguationData":[TD([[subQ2,-1.0]])],"derivedFrom":subQ1}),1.0]])]});}
            var Q69;
            {var subQ0=sQuery(id+"F0.wireOp",EDGE,"E31.right");var subQ1=sQuery(id+"F0.wireOp",EDGE,"E8");var subQ2=makeQuery(id+"F0.imprint","INTERSECT",VERTEX,{"derivedFrom":[subQ1,subQ0]});Q69=makeQuery(id+"F0.imprint","IMPRINT",FACE,{"disambiguationData":[TD([[makeQuery(id+"F0.imprint","IMPRINT",EDGE,{"disambiguationData":[TD([[subQ2,-1.0]])],"derivedFrom":subQ1}),1.0]])]});}
            var Q70;
            {var subQ0=sQuery(id+"F0.wireOp",EDGE,"E22.left");var subQ1=sQuery(id+"F0.wireOp",EDGE,"E20.top");var subQ2=makeQuery(id+"F0.imprint","INTERSECT",VERTEX,{"derivedFrom":[subQ1,subQ0]});Q70=makeQuery(id+"F0.imprint","IMPRINT",FACE,{"disambiguationData":[TD([[makeQuery(id+"F0.imprint","IMPRINT",EDGE,{"disambiguationData":[TD([[subQ2,-1.0]])],"derivedFrom":subQ1}),1.0]])]});}
            var Q71;
            {var subQ0=sQuery(id+"F0.wireOp",EDGE,"E31.left");var subQ1=sQuery(id+"F0.wireOp",EDGE,"E19.bottom");var subQ2=makeQuery(id+"F0.imprint","INTERSECT",VERTEX,{"derivedFrom":[subQ1,subQ0]});Q71=makeQuery(id+"F0.imprint","IMPRINT",FACE,{"disambiguationData":[TD([[makeQuery(id+"F0.imprint","IMPRINT",EDGE,{"disambiguationData":[TD([[subQ2,-1.0]])],"derivedFrom":subQ1}),-1.0]])]});}
            var Q72;
            {var subQ0=sQuery(id+"F0.wireOp",EDGE,"E27.left");var subQ1=sQuery(id+"F0.wireOp",EDGE,"E20.top");var subQ2=makeQuery(id+"F0.imprint","INTERSECT",VERTEX,{"derivedFrom":[subQ1,subQ0]});Q72=makeQuery(id+"F0.imprint","IMPRINT",FACE,{"disambiguationData":[TD([[makeQuery(id+"F0.imprint","IMPRINT",EDGE,{"disambiguationData":[TD([[subQ2,-1.0]])],"derivedFrom":subQ1}),1.0]])]});}
            var Q73;
            {var subQ0=sQuery(id+"F0.wireOp",EDGE,"E29.left");var subQ1=sQuery(id+"F0.wireOp",EDGE,"E20.top");var subQ2=makeQuery(id+"F0.imprint","INTERSECT",VERTEX,{"derivedFrom":[subQ1,subQ0]});Q73=makeQuery(id+"F0.imprint","IMPRINT",FACE,{"disambiguationData":[TD([[makeQuery(id+"F0.imprint","IMPRINT",EDGE,{"disambiguationData":[TD([[subQ2,-1.0]])],"derivedFrom":subQ1}),1.0]])]});}
            var Q74;
            {var subQ0=sQuery(id+"F0.wireOp",EDGE,"E29.left");var subQ1=sQuery(id+"F0.wireOp",EDGE,"E19.top");var subQ2=makeQuery(id+"F0.imprint","INTERSECT",VERTEX,{"derivedFrom":[subQ1,subQ0]});Q74=makeQuery(id+"F0.imprint","IMPRINT",FACE,{"disambiguationData":[TD([[makeQuery(id+"F0.imprint","IMPRINT",EDGE,{"disambiguationData":[TD([[subQ2,-1.0]])],"derivedFrom":subQ1}),-1.0]])]});}
            extrude(context, id + "F1", {"entities" : qUnion([Q0, Q1, Q2, Q3, Q4, Q5, Q6, Q7, Q8, Q9, Q10, Q11, Q12, Q13, Q14, Q15, Q16, Q17, Q18, Q19, Q20, Q21, Q22, Q23, Q24, Q25, Q26, Q27, Q28, Q29, Q30, Q31, Q32, Q33, Q34, Q35, Q36, Q37, Q38, Q39, Q40, Q41, Q42, Q43, Q44, Q45, Q46, Q47, Q48, Q49, Q50, Q51, Q52, Q53, Q54, Q55, Q56, Q57, Q58, Q59, Q60, Q61, Q62, Q63, Q64, Q65, Q66, Q67, Q68, Q69, Q70, Q71, Q72, Q73, Q74]), "depth" : 50.8 * mm});
        }
        {
            var Q0;
            Q0=makeQuery(id+"F1.opExtrude","CAP_FACE",FACE,{"disambiguationData":[OSD([sQuery(id+"F0.wireOp",EDGE,"E0"),sQuery(id+"F0.wireOp",EDGE,"E1"),sQuery(id+"F0.wireOp",EDGE,"E2"),sQuery(id+"F0.wireOp",EDGE,"E3"),sQuery(id+"F0.wireOp",EDGE,"E4"),sQuery(id+"F0.wireOp",EDGE,"E5"),sQuery(id+"F0.wireOp",EDGE,"E6"),sQuery(id+"F0.wireOp",EDGE,"E8"),sQuery(id+"F0.wireOp",EDGE,"E10"),sQuery(id+"F0.wireOp",EDGE,"E11"),sQuery(id+"F0.wireOp",EDGE,"E13"),sQuery(id+"F0.wireOp",EDGE,"E15"),sQuery(id+"F0.wireOp",EDGE,"E16"),sQuery(id+"F0.wireOp",EDGE,"E17"),sQuery(id+"F0.wireOp",EDGE,"E18"),sQuery(id+"F0.wireOp",EDGE,"E19.bottom"),sQuery(id+"F0.wireOp",EDGE,"E19.top"),sQuery(id+"F0.wireOp",EDGE,"E19.left"),sQuery(id+"F0.wireOp",EDGE,"E19.right"),sQuery(id+"F0.wireOp",EDGE,"E20.bottom"),sQuery(id+"F0.wireOp",EDGE,"E20.top"),sQuery(id+"F0.wireOp",EDGE,"E20.left"),sQuery(id+"F0.wireOp",EDGE,"E20.right"),sQuery(id+"F0.wireOp",EDGE,"E21.bottom"),sQuery(id+"F0.wireOp",EDGE,"E21.top"),sQuery(id+"F0.wireOp",EDGE,"E21.left"),sQuery(id+"F0.wireOp",EDGE,"E21.right"),sQuery(id+"F0.wireOp",EDGE,"E22.bottom"),sQuery(id+"F0.wireOp",EDGE,"E22.top"),sQuery(id+"F0.wireOp",EDGE,"E22.left"),sQuery(id+"F0.wireOp",EDGE,"E22.right"),sQuery(id+"F0.wireOp",EDGE,"E23.bottom"),sQuery(id+"F0.wireOp",EDGE,"E23.top"),sQuery(id+"F0.wireOp",EDGE,"E23.left"),sQuery(id+"F0.wireOp",EDGE,"E23.right"),sQuery(id+"F0.wireOp",EDGE,"E27.bottom"),sQuery(id+"F0.wireOp",EDGE,"E27.top"),sQuery(id+"F0.wireOp",EDGE,"E27.left"),sQuery(id+"F0.wireOp",EDGE,"E27.right"),sQuery(id+"F0.wireOp",EDGE,"E28.bottom"),sQuery(id+"F0.wireOp",EDGE,"E28.top"),sQuery(id+"F0.wireOp",EDGE,"E28.left"),sQuery(id+"F0.wireOp",EDGE,"E28.right"),sQuery(id+"F0.wireOp",EDGE,"E29.bottom"),sQuery(id+"F0.wireOp",EDGE,"E29.top"),sQuery(id+"F0.wireOp",EDGE,"E29.left"),sQuery(id+"F0.wireOp",EDGE,"E29.right"),sQuery(id+"F0.wireOp",EDGE,"E30.bottom"),sQuery(id+"F0.wireOp",EDGE,"E30.top"),sQuery(id+"F0.wireOp",EDGE,"NliR9Cyk-CJk0-Iiul-wSK4-aNZwnmZK0H1W.bottom"),sQuery(id+"F0.wireOp",EDGE,"NliR9Cyk-CJk0-Iiul-wSK4-aNZwnmZK0H1W.top")])],"isStart":false});
            var sketch = newSketch(context, id + "F2", { "sketchPlane" : qUnion([Q0])});
            skLineSegment(sketch, "E34.bottom", {"start": v(-2489.2, 1219.2) * mm, "end": v(-2387.6, 1219.2) * mm});
            skLineSegment(sketch, "E34.top", {"start": v(-2489.2, 0) * mm, "end": v(-2387.6, 0) * mm});
            skLineSegment(sketch, "E34.left", {"start": v(-2489.2, 1219.2) * mm, "end": v(-2489.2, 0) * mm});
            skLineSegment(sketch, "E34.right", {"start": v(-2387.6, 1219.2) * mm, "end": v(-2387.6, 0) * mm});
            skLineSegment(sketch, "E35.bottom", {"start": v(50.8, 1219.2) * mm, "end": v(-50.8, 1219.2) * mm});
            skLineSegment(sketch, "E35.top", {"start": v(50.8, 0) * mm, "end": v(-50.8, 0) * mm});
            skLineSegment(sketch, "E35.left", {"start": v(50.8, 1219.2) * mm, "end": v(50.8, 0) * mm});
            skLineSegment(sketch, "E35.right", {"start": v(-50.8, 1219.2) * mm, "end": v(-50.8, 0) * mm});
            skSolve(sketch);
        }
        {
            var Q0;
            Q0 = qSketchRegion(id + "F2", true);
            extrude(context, id + "F3", {"entities" : qUnion([Q0]), "operationType" : NewBodyOperationType.ADD, "depth" : 25.4 * mm});
        }
        {
            var Q0;
            Q0=makeQuery(id+"F1.opExtrude","CAP_FACE",FACE,{"disambiguationData":[OSD([sQuery(id+"F0.wireOp",EDGE,"E0"),sQuery(id+"F0.wireOp",EDGE,"E1"),sQuery(id+"F0.wireOp",EDGE,"E2"),sQuery(id+"F0.wireOp",EDGE,"E3"),sQuery(id+"F0.wireOp",EDGE,"E4"),sQuery(id+"F0.wireOp",EDGE,"E5"),sQuery(id+"F0.wireOp",EDGE,"E6"),sQuery(id+"F0.wireOp",EDGE,"E8"),sQuery(id+"F0.wireOp",EDGE,"E10"),sQuery(id+"F0.wireOp",EDGE,"E11"),sQuery(id+"F0.wireOp",EDGE,"E13"),sQuery(id+"F0.wireOp",EDGE,"E15"),sQuery(id+"F0.wireOp",EDGE,"E16"),sQuery(id+"F0.wireOp",EDGE,"E17"),sQuery(id+"F0.wireOp",EDGE,"E18"),sQuery(id+"F0.wireOp",EDGE,"E19.bottom"),sQuery(id+"F0.wireOp",EDGE,"E19.top"),sQuery(id+"F0.wireOp",EDGE,"E19.left"),sQuery(id+"F0.wireOp",EDGE,"E19.right"),sQuery(id+"F0.wireOp",EDGE,"E20.bottom"),sQuery(id+"F0.wireOp",EDGE,"E20.top"),sQuery(id+"F0.wireOp",EDGE,"E20.left"),sQuery(id+"F0.wireOp",EDGE,"E20.right"),sQuery(id+"F0.wireOp",EDGE,"E21.bottom"),sQuery(id+"F0.wireOp",EDGE,"E21.top"),sQuery(id+"F0.wireOp",EDGE,"E21.left"),sQuery(id+"F0.wireOp",EDGE,"E21.right"),sQuery(id+"F0.wireOp",EDGE,"E22.bottom"),sQuery(id+"F0.wireOp",EDGE,"E22.top"),sQuery(id+"F0.wireOp",EDGE,"E22.left"),sQuery(id+"F0.wireOp",EDGE,"E22.right"),sQuery(id+"F0.wireOp",EDGE,"E23.bottom"),sQuery(id+"F0.wireOp",EDGE,"E23.top"),sQuery(id+"F0.wireOp",EDGE,"E23.left"),sQuery(id+"F0.wireOp",EDGE,"E23.right"),sQuery(id+"F0.wireOp",EDGE,"E27.bottom"),sQuery(id+"F0.wireOp",EDGE,"E27.top"),sQuery(id+"F0.wireOp",EDGE,"E27.left"),sQuery(id+"F0.wireOp",EDGE,"E27.right"),sQuery(id+"F0.wireOp",EDGE,"E28.bottom"),sQuery(id+"F0.wireOp",EDGE,"E28.top"),sQuery(id+"F0.wireOp",EDGE,"E28.left"),sQuery(id+"F0.wireOp",EDGE,"E28.right"),sQuery(id+"F0.wireOp",EDGE,"E29.bottom"),sQuery(id+"F0.wireOp",EDGE,"E29.top"),sQuery(id+"F0.wireOp",EDGE,"E29.left"),sQuery(id+"F0.wireOp",EDGE,"E29.right"),sQuery(id+"F0.wireOp",EDGE,"E30.bottom"),sQuery(id+"F0.wireOp",EDGE,"E30.top"),sQuery(id+"F0.wireOp",EDGE,"NliR9Cyk-CJk0-Iiul-wSK4-aNZwnmZK0H1W.bottom"),sQuery(id+"F0.wireOp",EDGE,"NliR9Cyk-CJk0-Iiul-wSK4-aNZwnmZK0H1W.top")])],"isStart":true});
            var sketch = newSketch(context, id + "F4", { "sketchPlane" : qUnion([Q0])});
            skLineSegment(sketch, "E36.bottom", {"start": v(-50.8, 1219.2) * mm, "end": v(50.8, 1219.2) * mm});
            skLineSegment(sketch, "E36.top", {"start": v(-50.8, 0) * mm, "end": v(50.8, 0) * mm});
            skLineSegment(sketch, "E36.left", {"start": v(-50.8, 1219.2) * mm, "end": v(-50.8, 0) * mm});
            skLineSegment(sketch, "E36.right", {"start": v(50.8, 1219.2) * mm, "end": v(50.8, 0) * mm});
            skLineSegment(sketch, "E37.bottom", {"start": v(2387.6, 1219.2) * mm, "end": v(2489.2, 1219.2) * mm});
            skLineSegment(sketch, "E37.top", {"start": v(2387.6, 0) * mm, "end": v(2489.2, 0) * mm});
            skLineSegment(sketch, "E37.left", {"start": v(2387.6, 1219.2) * mm, "end": v(2387.6, 0) * mm});
            skLineSegment(sketch, "E37.right", {"start": v(2489.2, 1219.2) * mm, "end": v(2489.2, 0) * mm});
            skSolve(sketch);
        }
        {
            var Q0;
            Q0 = qSketchRegion(id + "F4", true);
            extrude(context, id + "F5", {"entities" : qUnion([Q0]), "operationType" : NewBodyOperationType.ADD, "depth" : 25.4 * mm});
        }
        {
            var Q0;
            Q0=makeQuery(id+"F3.opExtrude","CAP_EDGE",EDGE,{"disambiguationData":[OSD([sQuery(id+"F2.wireOp",EDGE,"E34.bottom")])],"isStart":false});
            var Q1;
            Q1=makeQuery(id+"F5.boolean.opBoolean","MERGE",EDGE,{"derivedFrom":[makeQuery(id+"F3.boolean.opBoolean","MERGE",EDGE,{"derivedFrom":[makeQuery(id+"F1.opExtrude","SWEPT_EDGE",EDGE,{"disambiguationData":[OSD([sQuery(id+"F0.wireOp",EDGE,"E15"),sQuery(id+"F0.wireOp",EDGE,"E16")])]}),makeQuery(id+"F3.opExtrude","SWEPT_EDGE",EDGE,{"disambiguationData":[OSD([sQuery(id+"F2.wireOp",EDGE,"E34.bottom"),sQuery(id+"F2.wireOp",EDGE,"E34.right")])]})]}),makeQuery(id+"F5.opExtrude","SWEPT_EDGE",EDGE,{"disambiguationData":[OSD([sQuery(id+"F4.wireOp",EDGE,"E37.bottom"),sQuery(id+"F4.wireOp",EDGE,"E37.left")])]})]});
            var Q2;
            Q2=makeQuery(id+"F5.opExtrude","CAP_EDGE",EDGE,{"disambiguationData":[OSD([sQuery(id+"F4.wireOp",EDGE,"E37.bottom")])],"isStart":false});
            var Q3;
            Q3=makeQuery(id+"F5.boolean.opBoolean","MERGE",EDGE,{"derivedFrom":[makeQuery(id+"F3.boolean.opBoolean","MERGE",EDGE,{"derivedFrom":[makeQuery(id+"F1.opExtrude","SWEPT_EDGE",EDGE,{"disambiguationData":[OSD([sQuery(id+"F0.wireOp",EDGE,"E16"),sQuery(id+"F0.wireOp",EDGE,"E17")])]}),makeQuery(id+"F3.opExtrude","SWEPT_EDGE",EDGE,{"disambiguationData":[OSD([sQuery(id+"F2.wireOp",EDGE,"E34.bottom"),sQuery(id+"F2.wireOp",EDGE,"E34.left")])]})]}),makeQuery(id+"F5.opExtrude","SWEPT_EDGE",EDGE,{"disambiguationData":[OSD([sQuery(id+"F4.wireOp",EDGE,"E37.bottom"),sQuery(id+"F4.wireOp",EDGE,"E37.right")])]})]});
            var Q4;
            Q4=makeQuery(id+"F3.opExtrude","CAP_EDGE",EDGE,{"disambiguationData":[OSD([sQuery(id+"F2.wireOp",EDGE,"E34.left")])],"isStart":false});
            var Q5;
            Q5=makeQuery(id+"F5.opExtrude","CAP_EDGE",EDGE,{"disambiguationData":[OSD([sQuery(id+"F4.wireOp",EDGE,"E37.right")])],"isStart":false});
            var Q6;
            Q6=makeQuery(id+"F3.opExtrude","CAP_EDGE",EDGE,{"disambiguationData":[OSD([sQuery(id+"F2.wireOp",EDGE,"E34.right")])],"isStart":false});
            var Q7;
            Q7=makeQuery(id+"F5.opExtrude","CAP_EDGE",EDGE,{"disambiguationData":[OSD([sQuery(id+"F4.wireOp",EDGE,"E37.left")])],"isStart":false});
            var Q8;
            Q8=makeQuery(id+"F5.opExtrude","CAP_EDGE",EDGE,{"disambiguationData":[OSD([sQuery(id+"F4.wireOp",EDGE,"E36.bottom")])],"isStart":false});
            var Q9;
            Q9=makeQuery(id+"F5.boolean.opBoolean","MERGE",EDGE,{"derivedFrom":[makeQuery(id+"F3.boolean.opBoolean","MERGE",EDGE,{"derivedFrom":[makeQuery(id+"F1.opExtrude","SWEPT_EDGE",EDGE,{"disambiguationData":[OSD([sQuery(id+"F0.wireOp",EDGE,"E2"),sQuery(id+"F0.wireOp",EDGE,"E3")])]}),makeQuery(id+"F3.opExtrude","SWEPT_EDGE",EDGE,{"disambiguationData":[OSD([sQuery(id+"F2.wireOp",EDGE,"E35.bottom"),sQuery(id+"F2.wireOp",EDGE,"E35.right")])]})]}),makeQuery(id+"F5.opExtrude","SWEPT_EDGE",EDGE,{"disambiguationData":[OSD([sQuery(id+"F4.wireOp",EDGE,"E36.bottom"),sQuery(id+"F4.wireOp",EDGE,"E36.right")])]})]});
            var Q10;
            Q10=makeQuery(id+"F5.boolean.opBoolean","MERGE",EDGE,{"derivedFrom":[makeQuery(id+"F3.boolean.opBoolean","MERGE",EDGE,{"derivedFrom":[makeQuery(id+"F1.opExtrude","SWEPT_EDGE",EDGE,{"disambiguationData":[OSD([sQuery(id+"F0.wireOp",EDGE,"E1"),sQuery(id+"F0.wireOp",EDGE,"E2")])]}),makeQuery(id+"F3.opExtrude","SWEPT_EDGE",EDGE,{"disambiguationData":[OSD([sQuery(id+"F2.wireOp",EDGE,"E35.bottom"),sQuery(id+"F2.wireOp",EDGE,"E35.left")])]})]}),makeQuery(id+"F5.opExtrude","SWEPT_EDGE",EDGE,{"disambiguationData":[OSD([sQuery(id+"F4.wireOp",EDGE,"E36.bottom"),sQuery(id+"F4.wireOp",EDGE,"E36.left")])]})]});
            var Q11;
            Q11=makeQuery(id+"F3.opExtrude","CAP_EDGE",EDGE,{"disambiguationData":[OSD([sQuery(id+"F2.wireOp",EDGE,"E35.bottom")])],"isStart":false});
            var Q12;
            Q12=makeQuery(id+"F3.opExtrude","CAP_EDGE",EDGE,{"disambiguationData":[OSD([sQuery(id+"F2.wireOp",EDGE,"E35.right")])],"isStart":false});
            var Q13;
            Q13=makeQuery(id+"F3.opExtrude","CAP_EDGE",EDGE,{"disambiguationData":[OSD([sQuery(id+"F2.wireOp",EDGE,"E35.left")])],"isStart":false});
            var Q14;
            Q14=makeQuery(id+"F5.opExtrude","CAP_EDGE",EDGE,{"disambiguationData":[OSD([sQuery(id+"F4.wireOp",EDGE,"E36.left")])],"isStart":false});
            var Q15;
            Q15=makeQuery(id+"F5.opExtrude","CAP_EDGE",EDGE,{"disambiguationData":[OSD([sQuery(id+"F4.wireOp",EDGE,"E36.right")])],"isStart":false});
            chamfer(context, id + "F6", {"entities" : qUnion([Q0, Q1, Q2, Q3, Q4, Q5, Q6, Q7, Q8, Q9, Q10, Q11, Q12, Q13, Q14, Q15]), "width" : 6.35 * mm, "tangentPropagation" : true});
        }
    });
